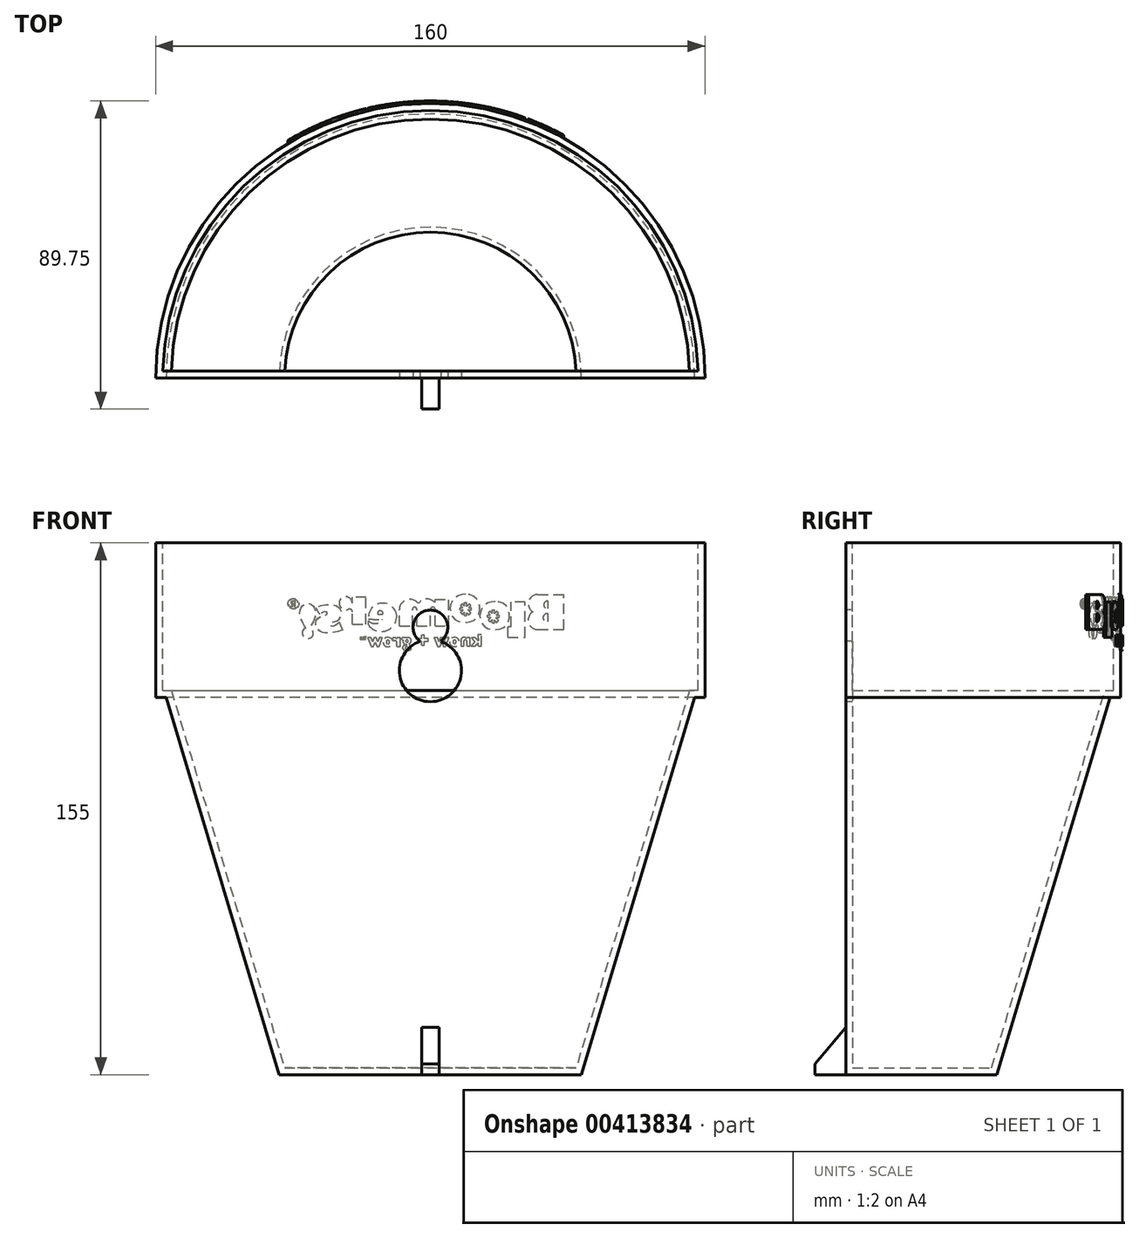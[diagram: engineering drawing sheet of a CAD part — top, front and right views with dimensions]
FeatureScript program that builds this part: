
annotation { "Feature Type Name" : "Feature", "Feature Type Description" : "" }
export const myFeature = defineFeature(function(context is Context, id is Id, definition is map)
    precondition{}
    {
        {
            var Q0;
            Q0=qCreatedBy(makeId("Front.planeOp"),FACE);
            var sketch = newSketch(context, id + "F0", { "sketchPlane" : qUnion([Q0])});
            skLineSegment(sketch, "E0", {"start": v(0, 63.42) * mm, "end": v(-80, 63.42) * mm});
            skLineSegment(sketch, "E1", {"start": v(-80, 63.42) * mm, "end": v(-80, 18.42) * mm});
            skLineSegment(sketch, "E2", {"start": v(0, -91.58) * mm, "end": v(-44, -91.58) * mm});
            skLineSegment(sketch, "E3", {"start": v(-80, 18.42) * mm, "end": v(-77, 18.42) * mm});
            skLineSegment(sketch, "E4", {"start": v(0, 63.42) * mm, "end": v(0, -91.58) * mm});
            skLineSegment(sketch, "E5", {"start": v(-77, 18.42) * mm, "end": v(-44, -91.58) * mm});
            skLineSegment(sketch, "E6.MirrorCS", {"start": v(0, 63.42) * mm, "end": v(80, 63.42) * mm});
            skLineSegment(sketch, "E7.MirrorCS", {"start": v(80, 63.42) * mm, "end": v(80, 18.42) * mm});
            skLineSegment(sketch, "E8.MirrorCS", {"start": v(80, 18.42) * mm, "end": v(77, 18.42) * mm});
            skLineSegment(sketch, "E9.MirrorCS", {"start": v(77, 18.42) * mm, "end": v(44, -91.58) * mm});
            skLineSegment(sketch, "E10.MirrorCS", {"start": v(0, -91.58) * mm, "end": v(44, -91.58) * mm});
            skSolve(sketch);
        }
        {
            var Q0;
            {var subQ0=sQuery(id+"F0.wireOp",EDGE,"E3");Q0=makeQuery(id+"F0.imprint","IMPRINT",FACE,{"disambiguationData":[TD([[makeQuery(id+"F0.imprint","IMPRINT",EDGE,{"derivedFrom":subQ0}),1.0]])]});}
            var Q1;
            {var subQ1=sQuery(id+"F0.wireOp",EDGE,"E0");Q1=makeQuery(id+"F0.imprint","IMPRINT",FACE,{"disambiguationData":[TD([[makeQuery(id+"F0.imprint","IMPRINT",EDGE,{"derivedFrom":subQ1}),1.0]])]});}
            var Q2;
            Q2=makeQuery(id+"F0.imprint","IMPRINT",FACE,{"disambiguationData":[TD([[makeQuery(id+"F0.imprint","IMPRINT",EDGE,{"derivedFrom":sQuery(id+"F0.wireOp",EDGE,"Kfnrekvc-ZjTY-c2iQ-cK4z-hKnBe4uEAVNk")}),1.0]])]});
            var Q3;
            Q3=sQuery(id+"F0.wireOp",EDGE,"E4");
            revolve(context, id + "F1", {"entities" : qUnion([Q0, Q1, Q2]), "axis" : qUnion([Q3]), "revolveType" : RevolveType.ONE_DIRECTION, "angle" : 180 * degree});
        }
        {
            var Q0;
            Q0=makeQuery(id+"FK2OT3XlAi37Aaq_1.splitOp","SPLIT",FACE,{"derivedFrom":makeQuery(id+"F1.opRevolve","SWEPT_FACE",FACE,{"disambiguationData":[OSD([sQuery(id+"F0.wireOp",EDGE,"E0")])]}),"isFromBackBody":true});
            shell(context, id + "F2", {"entities" : qUnion([Q0]), "thickness" : 2 * mm});
        }
        {
            var Q0;
            Q0=qCreatedBy(makeId("Front.planeOp"),FACE);
            var sketch = newSketch(context, id + "F3", { "sketchPlane" : qUnion([Q0])});
            skLineSegment(sketch, "E11.bottom", {"start": v(-2.5, -76.58) * mm, "end": v(2.5, -76.58) * mm});
            skLineSegment(sketch, "E11.top", {"start": v(-2.5, -91.58) * mm, "end": v(2.5, -91.58) * mm});
            skLineSegment(sketch, "E11.left", {"start": v(-2.5, -76.58) * mm, "end": v(-2.5, -91.58) * mm});
            skLineSegment(sketch, "E11.right", {"start": v(2.5, -76.58) * mm, "end": v(2.5, -91.58) * mm});
            skPoint(sketch, "E11.middle", {"position": v(0, -84.08) * mm});
            skSolve(sketch);
        }
        {
            var Q0;
            Q0=qSketchRegion(id+"F3",true);
            extrude(context, id + "F4", {"entities" : qUnion([Q0]), "operationType" : NewBodyOperationType.ADD, "depth" : 9 * mm});
        }
        {
            var Q0;
            Q0=qCreatedBy(makeId("Front.planeOp"),FACE);
            var sketch = newSketch(context, id + "F5", { "sketchPlane" : qUnion([Q0])});
            skCircle(sketch, "E12", {"center": v(0, 38.78) * mm, "radius": 5.05 * mm});
            skCircle(sketch, "E13", {"center": v(0, 26.17) * mm, "radius": 9.05 * mm});
            skSolve(sketch);
        }
        {
            var Q0;
            {var subQ0=sQuery(id+"F5.wireOp",EDGE,"E13");var subQ1=sQuery(id+"F5.wireOp",EDGE,"E12");var subQ2=makeQuery(id+"F5.imprint","INTERSECT",VERTEX,{"disambiguationData":[OD(0.0)],"derivedFrom":[subQ1,subQ0]});Q0=makeQuery(id+"F5.imprint","IMPRINT",FACE,{"disambiguationData":[TD([[makeQuery(id+"F5.imprint","IMPRINT",EDGE,{"disambiguationData":[TD([[subQ2,1.0]])],"derivedFrom":subQ1}),1.0]])]});}
            var Q1;
            {var subQ0=sQuery(id+"F5.wireOp",EDGE,"E13");var subQ1=sQuery(id+"F5.wireOp",EDGE,"E12");var subQ2=makeQuery(id+"F5.imprint","INTERSECT",VERTEX,{"disambiguationData":[OD(0.0)],"derivedFrom":[subQ1,subQ0]});Q1=makeQuery(id+"F5.imprint","IMPRINT",FACE,{"disambiguationData":[TD([[makeQuery(id+"F5.imprint","IMPRINT",EDGE,{"disambiguationData":[TD([[subQ2,-1.0]])],"derivedFrom":subQ1}),-1.0]])]});}
            var Q2;
            {var subQ0=sQuery(id+"F5.wireOp",EDGE,"E13");var subQ1=sQuery(id+"F5.wireOp",EDGE,"E12");var subQ2=makeQuery(id+"F5.imprint","INTERSECT",VERTEX,{"disambiguationData":[OD(0.0)],"derivedFrom":[subQ1,subQ0]});Q2=makeQuery(id+"F5.imprint","IMPRINT",FACE,{"disambiguationData":[TD([[makeQuery(id+"F5.imprint","IMPRINT",EDGE,{"disambiguationData":[TD([[subQ2,-1.0]])],"derivedFrom":subQ1}),1.0]])]});}
            var Q3;
            Q3=sQuery(id+"F5.wireOp",EDGE,"E12");
            var Q4;
            Q4=sQuery(id+"F5.wireOp",EDGE,"E13");
            extrude(context, id + "F6", {"entities" : qUnion([Q0, Q1, Q2]), "operationType" : NewBodyOperationType.REMOVE, "surfaceEntities" : qUnion([Q3, Q4]), "oppositeDirection" : true, "depth" : 10 * mm});
        }
        {
            var Q0;
            Q0=makeQuery(id+"F4.opExtrude","CAP_EDGE",EDGE,{"disambiguationData":[OSD([sQuery(id+"F3.wireOp",EDGE,"E11.bottom")])],"isStart":false});
            chamfer(context, id + "F7", {"entities" : qUnion([Q0]), "chamferType" : ChamferType.OFFSET_ANGLE, "width" : 10 * mm, "oppositeDirection" : false, "angle" : 50 * degree, "tangentPropagation" : true});
        }
        {
            var Q0;
            Q0=makeQuery(id+"F1.opRevolve","SWEPT_BODY",BODY,{"disambiguationData":[OSD([sQuery(id+"F0.wireOp",EDGE,"E0"),sQuery(id+"F0.wireOp",EDGE,"E1"),sQuery(id+"F0.wireOp",EDGE,"E2"),sQuery(id+"F0.wireOp",EDGE,"E3"),sQuery(id+"F0.wireOp",EDGE,"E4"),sQuery(id+"F0.wireOp",EDGE,"E5")])]});
            transform(context, id + "F8", {"entities" : qUnion([Q0]), "transformType" : TransformType.TRANSLATION_3D, "dx" : 0 * mm, "dy" : 0 * mm, "dz" : -7 * mm, "makeCopy" : false});
        }
        {
            var Q0;
            Q0=makeQuery(id+"F2.opShell","OFFSET_FACE",FACE,{"disambiguationData":[OSD([sQuery(id+"F0.wireOp",EDGE,"E0"),sQuery(id+"F0.wireOp",EDGE,"E1"),sQuery(id+"F0.wireOp",EDGE,"E2"),sQuery(id+"F0.wireOp",EDGE,"E3"),sQuery(id+"F0.wireOp",EDGE,"E4"),sQuery(id+"F0.wireOp",EDGE,"E5")])]});
            cPlane(context, id + "F9", {"entities" : qUnion([Q0]), "cplaneType" : CPlaneType.OFFSET, "offset" : 78.9 * mm, "width" : 150 * mm, "height" : 150 * mm});
        }
        {
            var Q0;
            Q0=qCreatedBy(id+"F9.planeOp",FACE);
            var sketch = newSketch(context, id + "F10", { "sketchPlane" : qUnion([Q0])});
            skLineSegment(sketch, "E14", {"start": v(-38.93, 41.35) * mm, "end": v(-38.93, 31.1) * mm});
            skLineSegment(sketch, "E15", {"start": v(-38.93, 31.1) * mm, "end": v(-31.26, 31.1) * mm});
            skLineSegment(sketch, "E16", {"start": v(-38.93, 41.35) * mm, "end": v(-31.26, 41.35) * mm});
            skArc(sketch, "E17", {"start": v(-29.86, 36.3) * mm, "mid": v(-28.64, 39.36) * mm, "end": v(-31.26, 41.35) * mm});
            skArc(sketch, "E18", {"start": v(-31.26, 31.1) * mm, "mid": v(-28.56, 33.17) * mm, "end": v(-29.86, 36.3) * mm});
            skLineSegment(sketch, "E19", {"start": v(-34.3, 39.39) * mm, "end": v(-34.3, 37.24) * mm});
            skArc(sketch, "E20", {"start": v(-34.3, 37.24) * mm, "mid": v(-33, 38.32) * mm, "end": v(-34.3, 39.39) * mm});
            skArc(sketch, "E21", {"start": v(-34.3, 33.47) * mm, "mid": v(-32.82, 34.59) * mm, "end": v(-34.3, 35.7) * mm});
            skLineSegment(sketch, "E22.trimOffspring", {"start": v(-34.3, 35.7) * mm, "end": v(-34.3, 33.47) * mm});
            skLineSegment(sketch, "E23", {"start": v(-27.58, 39.2) * mm, "end": v(-27.58, 28.9) * mm});
            skLineSegment(sketch, "E24", {"start": v(-27.58, 28.9) * mm, "end": v(-22.58, 28.9) * mm});
            skLineSegment(sketch, "E25", {"start": v(-22.58, 28.9) * mm, "end": v(-22.58, 31.98) * mm});
            skLineSegment(sketch, "E26", {"start": v(-22.58, 31.98) * mm, "end": v(-23.52, 31.98) * mm});
            skLineSegment(sketch, "E27", {"start": v(-23.52, 31.98) * mm, "end": v(-23.52, 39.2) * mm});
            skLineSegment(sketch, "E28", {"start": v(-23.52, 39.2) * mm, "end": v(-27.58, 39.2) * mm});
            skFitSpline(sketch, "E29", {"points": [v(-18.97, 39.3) * mm, v(-20.87, 38.92) * mm, v(-22.46, 37.44) * mm, v(-22.99, 35.82) * mm, v(-22.97, 34.09) * mm, v(-22.03, 32.34) * mm, v(-20.21, 31.27) * mm, v(-18.57, 31.14) * mm, v(-16.6, 31.5) * mm, v(-14.9, 33.15) * mm, v(-14.42, 35.37) * mm, v(-14.96, 37.3) * mm, v(-16.45, 38.75) * mm, v(-18.2, 39.28) * mm, v(-18.97, 39.3) * mm]});
            skLineSegment(sketch, "E30.bottom", {"start": v(-18.65, 36.9) * mm, "end": v(-18, 36.9) * mm});
            skLineSegment(sketch, "E30.top", {"start": v(-18.65, 33.13) * mm, "end": v(-18, 33.13) * mm});
            skLineSegment(sketch, "E30.left", {"start": v(-18.65, 36.9) * mm, "end": v(-18.65, 35.74) * mm});
            skLineSegment(sketch, "E30.right", {"start": v(-18, 36.9) * mm, "end": v(-18, 35.82) * mm});
            skLineSegment(sketch, "E31.bottom", {"start": v(-20.04, 35.3) * mm, "end": v(-19.23, 35.3) * mm});
            skLineSegment(sketch, "E31.top", {"start": v(-20.04, 34.7) * mm, "end": v(-19.05, 34.7) * mm});
            skLineSegment(sketch, "E31.left", {"start": v(-20.04, 35.3) * mm, "end": v(-20.04, 34.7) * mm});
            skLineSegment(sketch, "E31.right", {"start": v(-16.69, 35.3) * mm, "end": v(-16.69, 34.7) * mm});
            skLineSegment(sketch, "E32", {"start": v(-19.87, 35.97) * mm, "end": v(-19.23, 35.3) * mm});
            skLineSegment(sketch, "E33", {"start": v(-17.4, 33.43) * mm, "end": v(-16.88, 33.92) * mm});
            skLineSegment(sketch, "E34", {"start": v(-19.35, 36.45) * mm, "end": v(-19.87, 35.97) * mm});
            skLineSegment(sketch, "E35", {"start": v(-19.87, 33.85) * mm, "end": v(-19.25, 33.22) * mm});
            skLineSegment(sketch, "E36", {"start": v(-19.25, 33.22) * mm, "end": v(-18.65, 33.9) * mm});
            skLineSegment(sketch, "E37", {"start": v(-16.84, 35.97) * mm, "end": v(-17.39, 36.45) * mm});
            skLineSegment(sketch, "E38", {"start": v(-17.39, 36.45) * mm, "end": v(-18, 35.82) * mm});
            skLineSegment(sketch, "E39.trimOffspring", {"start": v(-18.65, 35.74) * mm, "end": v(-19.35, 36.45) * mm});
            skLineSegment(sketch, "E40.trimOffspring", {"start": v(-19.05, 34.7) * mm, "end": v(-19.87, 33.85) * mm});
            skLineSegment(sketch, "E41.trimOffspring", {"start": v(-18, 34.04) * mm, "end": v(-17.4, 33.43) * mm});
            skLineSegment(sketch, "E42.trimOffspring", {"start": v(-18.65, 33.9) * mm, "end": v(-18.65, 33.13) * mm});
            skLineSegment(sketch, "E43.trimOffspring", {"start": v(-18, 34.04) * mm, "end": v(-18, 33.13) * mm});
            skLineSegment(sketch, "E44.trimOffspring", {"start": v(-17.42, 35.3) * mm, "end": v(-16.84, 35.97) * mm});
            skLineSegment(sketch, "E45.trimOffspring", {"start": v(-17.42, 35.3) * mm, "end": v(-16.69, 35.3) * mm});
            skLineSegment(sketch, "E46.trimOffspring", {"start": v(-17.65, 34.7) * mm, "end": v(-16.69, 34.7) * mm});
            skFitSpline(sketch, "E47", {"points": [v(-10.3, 41.42) * mm, v(-12.2, 41.04) * mm, v(-13.79, 39.56) * mm, v(-14.32, 37.94) * mm, v(-14.3, 36.2) * mm, v(-13.36, 34.46) * mm, v(-11.55, 33.39) * mm, v(-9.9, 33.26) * mm, v(-7.94, 33.62) * mm, v(-6.23, 35.27) * mm, v(-5.76, 37.49) * mm, v(-6.3, 39.41) * mm, v(-7.79, 40.86) * mm, v(-9.54, 41.4) * mm, v(-10.3, 41.42) * mm]});
            skLineSegment(sketch, "E48", {"start": v(-17.65, 34.7) * mm, "end": v(-16.88, 33.92) * mm});
            skLineSegment(sketch, "E49.bottom", {"start": v(-10.58, 39.06) * mm, "end": v(-9.92, 39.06) * mm});
            skLineSegment(sketch, "E49.top", {"start": v(-10.58, 35.28) * mm, "end": v(-9.92, 35.28) * mm});
            skLineSegment(sketch, "E49.left", {"start": v(-10.58, 39.06) * mm, "end": v(-10.58, 37.9) * mm});
            skLineSegment(sketch, "E49.right", {"start": v(-9.92, 39.06) * mm, "end": v(-9.92, 37.97) * mm});
            skLineSegment(sketch, "E50.bottom", {"start": v(-11.97, 37.46) * mm, "end": v(-11.15, 37.46) * mm});
            skLineSegment(sketch, "E50.top", {"start": v(-11.97, 36.86) * mm, "end": v(-10.98, 36.86) * mm});
            skLineSegment(sketch, "E50.left", {"start": v(-11.97, 37.46) * mm, "end": v(-11.97, 36.86) * mm});
            skLineSegment(sketch, "E50.right", {"start": v(-8.61, 37.46) * mm, "end": v(-8.61, 36.86) * mm});
            skLineSegment(sketch, "E51", {"start": v(-11.8, 38.12) * mm, "end": v(-11.15, 37.46) * mm});
            skLineSegment(sketch, "E52", {"start": v(-9.32, 35.58) * mm, "end": v(-8.81, 36.08) * mm});
            skLineSegment(sketch, "E53", {"start": v(-11.27, 38.6) * mm, "end": v(-11.8, 38.12) * mm});
            skLineSegment(sketch, "E54", {"start": v(-11.8, 36) * mm, "end": v(-11.18, 35.37) * mm});
            skLineSegment(sketch, "E55", {"start": v(-11.18, 35.37) * mm, "end": v(-10.58, 36.05) * mm});
            skLineSegment(sketch, "E56", {"start": v(-8.76, 38.12) * mm, "end": v(-9.31, 38.6) * mm});
            skLineSegment(sketch, "E57", {"start": v(-9.31, 38.6) * mm, "end": v(-9.92, 37.97) * mm});
            skLineSegment(sketch, "E58.trimOffspring", {"start": v(-10.58, 37.9) * mm, "end": v(-11.27, 38.6) * mm});
            skLineSegment(sketch, "E59.trimOffspring", {"start": v(-10.98, 36.86) * mm, "end": v(-11.8, 36) * mm});
            skLineSegment(sketch, "E60.trimOffspring", {"start": v(-9.92, 36.2) * mm, "end": v(-9.32, 35.58) * mm});
            skLineSegment(sketch, "E61.trimOffspring", {"start": v(-10.58, 36.05) * mm, "end": v(-10.58, 35.28) * mm});
            skLineSegment(sketch, "E62.trimOffspring", {"start": v(-9.92, 36.2) * mm, "end": v(-9.92, 35.28) * mm});
            skLineSegment(sketch, "E63.trimOffspring", {"start": v(-9.34, 37.46) * mm, "end": v(-8.76, 38.12) * mm});
            skLineSegment(sketch, "E64.trimOffspring", {"start": v(-9.34, 37.46) * mm, "end": v(-8.61, 37.46) * mm});
            skLineSegment(sketch, "E65.trimOffspring", {"start": v(-9.58, 36.86) * mm, "end": v(-8.61, 36.86) * mm});
            skLineSegment(sketch, "E66", {"start": v(-9.58, 36.86) * mm, "end": v(-8.81, 36.08) * mm});
            skLineSegment(sketch, "E67", {"start": v(-5.38, 32.17) * mm, "end": v(-5.38, 39.97) * mm});
            skLineSegment(sketch, "E68", {"start": v(-5.38, 39.97) * mm, "end": v(-1.39, 39.97) * mm});
            skLineSegment(sketch, "E69", {"start": v(-1.39, 39.97) * mm, "end": v(-1.39, 39) * mm});
            skLineSegment(sketch, "E70", {"start": v(-5.38, 32.17) * mm, "end": v(-1.38, 32.17) * mm});
            skLineSegment(sketch, "E71", {"start": v(-1.38, 32.17) * mm, "end": v(-1.38, 36.98) * mm});
            skLineSegment(sketch, "E72", {"start": v(0, 36.98) * mm, "end": v(0, 32.17) * mm});
            skLineSegment(sketch, "E73", {"start": v(0, 32.17) * mm, "end": v(3.95, 32.17) * mm});
            skLineSegment(sketch, "E74", {"start": v(3.95, 32.17) * mm, "end": v(3.95, 36.98) * mm});
            skLineSegment(sketch, "E75", {"start": v(5.25, 36.98) * mm, "end": v(5.25, 32.17) * mm});
            skLineSegment(sketch, "E76", {"start": v(5.25, 32.17) * mm, "end": v(9.02, 32.17) * mm});
            skLineSegment(sketch, "E77", {"start": v(9.02, 32.17) * mm, "end": v(9.02, 36.98) * mm});
            skArc(sketch, "E78", {"start": v(5.25, 36.98) * mm, "mid": v(4.6, 37.63) * mm, "end": v(3.95, 36.98) * mm});
            skArc(sketch, "E79", {"start": v(0, 36.98) * mm, "mid": v(-0.69, 37.67) * mm, "end": v(-1.38, 36.98) * mm});
            skArc(sketch, "E80", {"start": v(3.53, 38.66) * mm, "mid": v(1.15, 40.01) * mm, "end": v(-1.39, 39) * mm});
            skArc(sketch, "E81", {"start": v(9.02, 36.98) * mm, "mid": v(6.9, 39.85) * mm, "end": v(3.53, 38.66) * mm});
            skArc(sketch, "E82", {"start": v(13.95, 34.1) * mm, "mid": v(15.9, 32.9) * mm, "end": v(18.03, 33.72) * mm});
            skArc(sketch, "E83", {"start": v(9.77, 35.2) * mm, "mid": v(12.91, 30.78) * mm, "end": v(18.06, 32.5) * mm});
            skArc(sketch, "E84", {"start": v(18.03, 34.17) * mm, "mid": v(14.4, 38.8) * mm, "end": v(9.77, 35.2) * mm});
            skLineSegment(sketch, "E85", {"start": v(13.95, 34.1) * mm, "end": v(18.03, 34.17) * mm});
            skLineSegment(sketch, "E86", {"start": v(13.9, 35.57) * mm, "end": v(15.36, 35.6) * mm});
            skArc(sketch, "E87", {"start": v(15.36, 35.6) * mm, "mid": v(14.6, 36.63) * mm, "end": v(13.9, 35.57) * mm});
            skLineSegment(sketch, "E88", {"start": v(18.03, 33.72) * mm, "end": v(18.06, 32.5) * mm});
            skLineSegment(sketch, "E89", {"start": v(22.73, 38.77) * mm, "end": v(22.73, 40.55) * mm});
            skLineSegment(sketch, "E90", {"start": v(22.73, 40.55) * mm, "end": v(18.72, 40.58) * mm});
            skLineSegment(sketch, "E91", {"start": v(18.72, 40.58) * mm, "end": v(18.72, 32.74) * mm});
            skLineSegment(sketch, "E92", {"start": v(18.72, 32.74) * mm, "end": v(22.7, 32.74) * mm});
            skLineSegment(sketch, "E93", {"start": v(22.7, 32.74) * mm, "end": v(22.7, 36.3) * mm});
            skArc(sketch, "E94", {"start": v(23.94, 36.98) * mm, "mid": v(26.24, 39.84) * mm, "end": v(22.73, 38.77) * mm});
            skArc(sketch, "E95", {"start": v(23.94, 36.98) * mm, "mid": v(23.11, 37) * mm, "end": v(22.7, 36.3) * mm});
            skLineSegment(sketch, "E96", {"start": v(33.3, 37.45) * mm, "end": v(32.27, 35.62) * mm});
            skFitSpline(sketch, "E97", {"points": [v(33.3, 37.45) * mm, v(32.36, 37.96) * mm, v(31.25, 38.2) * mm, v(30.16, 38.3) * mm, v(28.65, 38.26) * mm, v(27.14, 37.83) * mm, v(26.29, 37.06) * mm, v(25.86, 36.05) * mm, v(26.07, 34.84) * mm, v(26.79, 33.99) * mm, v(28.33, 33.35) * mm, v(29.12, 33.1) * mm, v(29.36, 32.85) * mm, v(29.3, 32.47) * mm, v(29, 32.12) * mm, v(28.48, 32.1) * mm, v(27.57, 32.38) * mm, v(26.88, 32.96) * mm, v(26.6, 33.22) * mm, v(26.49, 33.3) * mm], "startDerivative": vector(-15.65, 9.87) * mm, "endDerivative": vector(-4.84, 3.4) * mm});
            skFitSpline(sketch, "E98", {"points": [v(32.27, 35.62) * mm, v(31.94, 35.79) * mm, v(31.56, 36.06) * mm, v(31.13, 36.28) * mm, v(30.73, 36.4) * mm, v(30.1, 36.28) * mm, v(29.89, 35.88) * mm, v(30.08, 35.62) * mm, v(30.64, 35.32) * mm, v(31.42, 35.1) * mm, v(32.1, 34.87) * mm, v(32.63, 34.52) * mm, v(33.07, 34.09) * mm, v(33.37, 33.46) * mm, v(33.46, 33) * mm, v(33.46, 32.48) * mm, v(33.31, 31.72) * mm, v(32.8, 31.07) * mm, v(32.27, 30.71) * mm, v(31.46, 30.26) * mm, v(30.44, 30.1) * mm, v(29.25, 30.17) * mm, v(28.56, 30.21) * mm, v(27.53, 30.4) * mm, v(26.65, 30.67) * mm, v(26.13, 30.83) * mm, v(25.52, 31) * mm, v(24, 31.52) * mm], "startDerivative": vector(-12.22, 5.14) * mm, "endDerivative": vector(-29.8, 10.92) * mm});
            skLineSegment(sketch, "E99", {"start": v(26.49, 33.3) * mm, "end": v(25.52, 31) * mm});
            skFitSpline(sketch, "E100", {"points": [v(35.16, 31.53) * mm, v(34.54, 32.68) * mm, v(33.94, 33.8) * mm, v(33.6, 34.86) * mm, v(33.49, 36.06) * mm, v(33.7, 37.34) * mm, v(34.55, 38.4) * mm, v(35.36, 38.83) * mm, v(36.02, 38.89) * mm, v(36.86, 38.44) * mm, v(37.6, 37.54) * mm, v(38.02, 36.55) * mm, v(37.98, 35.4) * mm, v(37.68, 34.14) * mm, v(37.17, 33.21) * mm, v(36.7, 32.27) * mm, v(36.3, 31.56) * mm, v(36.34, 31.34) * mm], "startDerivative": vector(-9.25, 17.51) * mm, "endDerivative": vector(7.08, -5.7) * mm});
            skFitSpline(sketch, "E101", {"points": [v(35.16, 31.53) * mm, v(34.67, 31.23) * mm, v(34.3, 30.83) * mm, v(34.1, 30) * mm, v(34.28, 29.4) * mm, v(34.62, 28.94) * mm, v(35.02, 28.64) * mm, v(35.5, 28.5) * mm, v(36.33, 28.63) * mm, v(37.12, 29.37) * mm, v(37.32, 30.35) * mm, v(37.03, 31) * mm, v(36.66, 31.33) * mm, v(36.3, 31.56) * mm], "startDerivative": vector(-7.2, -4.04) * mm, "endDerivative": vector(-5.92, 3.66) * mm});
            skLineSegment(sketch, "E102", {"start": v(-13.86, 29.67) * mm, "end": v(-14.85, 29.67) * mm});
            skLineSegment(sketch, "E103", {"start": v(-14.85, 29.67) * mm, "end": v(-14.85, 26.29) * mm});
            skLineSegment(sketch, "E104", {"start": v(-14.85, 26.29) * mm, "end": v(-13.95, 26.29) * mm});
            skLineSegment(sketch, "E105", {"start": v(-13.95, 26.29) * mm, "end": v(-13.95, 27.28) * mm});
            skLineSegment(sketch, "E106", {"start": v(-13.95, 27.28) * mm, "end": v(-13.01, 26.29) * mm});
            skLineSegment(sketch, "E107", {"start": v(-13.01, 26.29) * mm, "end": v(-11.85, 26.29) * mm});
            skLineSegment(sketch, "E108", {"start": v(-11.85, 26.29) * mm, "end": v(-12.9, 27.58) * mm});
            skLineSegment(sketch, "E109", {"start": v(-12.9, 27.58) * mm, "end": v(-11.98, 28.72) * mm});
            skLineSegment(sketch, "E110", {"start": v(-11.98, 28.72) * mm, "end": v(-13.1, 28.72) * mm});
            skLineSegment(sketch, "E111", {"start": v(-13.1, 28.72) * mm, "end": v(-13.95, 27.88) * mm});
            skLineSegment(sketch, "E112", {"start": v(-13.95, 27.88) * mm, "end": v(-13.86, 29.67) * mm});
            skLineSegment(sketch, "E113", {"start": v(-11.59, 26.29) * mm, "end": v(-10.62, 26.29) * mm});
            skLineSegment(sketch, "E114", {"start": v(-10.62, 26.29) * mm, "end": v(-10.62, 27.77) * mm});
            skLineSegment(sketch, "E115", {"start": v(-9.77, 27.88) * mm, "end": v(-9.77, 26.29) * mm});
            skLineSegment(sketch, "E116", {"start": v(-9.77, 26.29) * mm, "end": v(-8.9, 26.29) * mm});
            skLineSegment(sketch, "E117", {"start": v(-8.9, 26.29) * mm, "end": v(-8.95, 28.42) * mm});
            skLineSegment(sketch, "E118", {"start": v(-10.49, 28.6) * mm, "end": v(-10.62, 28.6) * mm});
            skLineSegment(sketch, "E119", {"start": v(-10.62, 28.6) * mm, "end": v(-10.62, 28.76) * mm});
            skLineSegment(sketch, "E120", {"start": v(-10.62, 28.76) * mm, "end": v(-11.61, 28.76) * mm});
            skLineSegment(sketch, "E121", {"start": v(-11.61, 28.76) * mm, "end": v(-11.59, 26.29) * mm});
            skEllipse(sketch, "E122", {"center": v(-7.04, 27.54) * mm, "majorRadius": 0.56 * mm, "minorRadius": 0.44 * mm, "majorAxis": v(0, -1)});
            skEllipse(sketch, "E123", {"center": v(-7.04, 27.54) * mm, "majorRadius": 1.33 * mm, "minorRadius": 1.47 * mm, "majorAxis": v(0.05, -1)});
            skLineSegment(sketch, "E124", {"start": v(-4.42, 28.79) * mm, "end": v(-5.45, 28.79) * mm});
            skLineSegment(sketch, "E125", {"start": v(-5.45, 28.79) * mm, "end": v(-4.45, 26.23) * mm});
            skLineSegment(sketch, "E126", {"start": v(-4.45, 26.23) * mm, "end": v(-3.77, 26.23) * mm});
            skLineSegment(sketch, "E127", {"start": v(-3.77, 26.23) * mm, "end": v(-3.28, 27.38) * mm});
            skLineSegment(sketch, "E128", {"start": v(-3.28, 27.38) * mm, "end": v(-2.82, 26.22) * mm});
            skLineSegment(sketch, "E129", {"start": v(-2.82, 26.22) * mm, "end": v(-2.1, 26.22) * mm});
            skLineSegment(sketch, "E130", {"start": v(-2.1, 26.22) * mm, "end": v(-1.1, 28.75) * mm});
            skLineSegment(sketch, "E131", {"start": v(-1.1, 28.75) * mm, "end": v(-2.15, 28.75) * mm});
            skLineSegment(sketch, "E132", {"start": v(-2.15, 28.75) * mm, "end": v(-2.48, 27.64) * mm});
            skLineSegment(sketch, "E133", {"start": v(-2.48, 27.64) * mm, "end": v(-2.9, 28.75) * mm});
            skLineSegment(sketch, "E134", {"start": v(-2.9, 28.75) * mm, "end": v(-3.65, 28.75) * mm});
            skLineSegment(sketch, "E135", {"start": v(-3.65, 28.75) * mm, "end": v(-4.02, 27.66) * mm});
            skLineSegment(sketch, "E136", {"start": v(-4.02, 27.66) * mm, "end": v(-4.42, 28.79) * mm});
            skLineSegment(sketch, "E137", {"start": v(2.5, 29.58) * mm, "end": v(1.8, 29.58) * mm});
            skLineSegment(sketch, "E138", {"start": v(1.8, 29.58) * mm, "end": v(1.8, 28.47) * mm});
            skLineSegment(sketch, "E139", {"start": v(1.8, 28.47) * mm, "end": v(0.59, 28.47) * mm});
            skLineSegment(sketch, "E140", {"start": v(0.59, 28.47) * mm, "end": v(0.59, 27.74) * mm});
            skLineSegment(sketch, "E141", {"start": v(0.59, 27.74) * mm, "end": v(1.77, 27.74) * mm});
            skLineSegment(sketch, "E142", {"start": v(1.77, 27.74) * mm, "end": v(1.77, 26.58) * mm});
            skLineSegment(sketch, "E143", {"start": v(1.77, 26.58) * mm, "end": v(2.5, 26.58) * mm});
            skLineSegment(sketch, "E144", {"start": v(2.5, 26.58) * mm, "end": v(2.5, 27.74) * mm});
            skLineSegment(sketch, "E145", {"start": v(2.5, 27.74) * mm, "end": v(3.63, 27.74) * mm});
            skLineSegment(sketch, "E146", {"start": v(3.63, 27.74) * mm, "end": v(3.63, 28.45) * mm});
            skLineSegment(sketch, "E147", {"start": v(3.63, 28.45) * mm, "end": v(2.5, 28.45) * mm});
            skLineSegment(sketch, "E148", {"start": v(2.5, 28.45) * mm, "end": v(2.5, 29.58) * mm});
            skEllipse(sketch, "E149", {"center": v(12.37, 27.5) * mm, "majorRadius": 0.56 * mm, "minorRadius": 0.47 * mm, "majorAxis": v(0, -1)});
            skEllipse(sketch, "E150", {"center": v(12.37, 27.5) * mm, "majorRadius": 1.38 * mm, "minorRadius": 1.44 * mm, "majorAxis": v(0, -1)});
            skEllipse(sketch, "E151", {"center": v(6.82, 27.81) * mm, "majorRadius": 0.35 * mm, "minorRadius": 0.38 * mm, "majorAxis": v(0, -1)});
            skEllipse(sketch, "E152", {"center": v(6.86, 25.77) * mm, "majorRadius": 0.5 * mm, "minorRadius": 0.27 * mm, "majorAxis": v(1, 0)});
            skLineSegment(sketch, "E153", {"start": v(9.75, 28.76) * mm, "end": v(8.72, 28.76) * mm});
            skLineSegment(sketch, "E154", {"start": v(8.72, 28.76) * mm, "end": v(8.72, 26.23) * mm});
            skLineSegment(sketch, "E155", {"start": v(8.72, 26.23) * mm, "end": v(9.77, 26.23) * mm});
            skLineSegment(sketch, "E156", {"start": v(9.77, 26.23) * mm, "end": v(9.77, 27.57) * mm});
            skLineSegment(sketch, "E157", {"start": v(16.42, 28.76) * mm, "end": v(15.75, 28.76) * mm});
            skLineSegment(sketch, "E158", {"start": v(15.75, 28.76) * mm, "end": v(15.33, 27.62) * mm});
            skLineSegment(sketch, "E159", {"start": v(15.33, 27.62) * mm, "end": v(14.91, 28.77) * mm});
            skLineSegment(sketch, "E160", {"start": v(14.91, 28.77) * mm, "end": v(14, 28.77) * mm});
            skLineSegment(sketch, "E161", {"start": v(14, 28.77) * mm, "end": v(14.91, 26.25) * mm});
            skLineSegment(sketch, "E162", {"start": v(14.91, 26.25) * mm, "end": v(15.58, 26.25) * mm});
            skLineSegment(sketch, "E163", {"start": v(15.58, 26.25) * mm, "end": v(16.06, 27.35) * mm});
            skLineSegment(sketch, "E164", {"start": v(16.06, 27.35) * mm, "end": v(16.6, 26.24) * mm});
            skLineSegment(sketch, "E165", {"start": v(16.6, 26.24) * mm, "end": v(17.25, 26.24) * mm});
            skLineSegment(sketch, "E166", {"start": v(17.25, 26.24) * mm, "end": v(18.26, 28.77) * mm});
            skLineSegment(sketch, "E167", {"start": v(18.26, 28.77) * mm, "end": v(17.24, 28.77) * mm});
            skLineSegment(sketch, "E168", {"start": v(17.24, 28.77) * mm, "end": v(16.82, 27.63) * mm});
            skLineSegment(sketch, "E169", {"start": v(16.82, 27.63) * mm, "end": v(16.42, 28.76) * mm});
            skArc(sketch, "E170", {"start": v(-9.77, 27.88) * mm, "mid": v(-10.23, 28.08) * mm, "end": v(-10.62, 27.77) * mm});
            skArc(sketch, "E171", {"start": v(-8.95, 28.42) * mm, "mid": v(-9.68, 28.85) * mm, "end": v(-10.49, 28.6) * mm});
            skLineSegment(sketch, "E172", {"start": v(9.75, 28.76) * mm, "end": v(9.75, 28.32) * mm});
            skLineSegment(sketch, "E173", {"start": v(10.97, 28.72) * mm, "end": v(10.69, 27.75) * mm});
            skArc(sketch, "E174", {"start": v(10.97, 28.72) * mm, "mid": v(10.29, 28.75) * mm, "end": v(9.75, 28.32) * mm});
            skArc(sketch, "E175", {"start": v(10.69, 27.75) * mm, "mid": v(10.2, 27.84) * mm, "end": v(9.77, 27.57) * mm});
            skLineSegment(sketch, "E176", {"start": v(8.25, 28.14) * mm, "end": v(8.25, 28.77) * mm});
            skLineSegment(sketch, "E177", {"start": v(8.25, 28.77) * mm, "end": v(6.33, 28.77) * mm});
            skArc(sketch, "E178", {"start": v(6.33, 28.77) * mm, "mid": v(5.61, 27.95) * mm, "end": v(6.19, 27.03) * mm});
            skArc(sketch, "E179", {"start": v(6.83, 26.9) * mm, "mid": v(7.8, 27.15) * mm, "end": v(7.96, 28.14) * mm});
            skLineSegment(sketch, "E180", {"start": v(7.96, 28.14) * mm, "end": v(8.25, 28.14) * mm});
            skLineSegment(sketch, "E181", {"start": v(6.83, 26.9) * mm, "end": v(6.83, 26.6) * mm});
            skLineSegment(sketch, "E182", {"start": v(6.83, 26.6) * mm, "end": v(7.57, 26.6) * mm});
            skArc(sketch, "E183", {"start": v(6.19, 27.03) * mm, "mid": v(5.96, 26.73) * mm, "end": v(6.04, 26.36) * mm});
            skArc(sketch, "E184", {"start": v(6.04, 26.36) * mm, "mid": v(5.52, 25.75) * mm, "end": v(6.04, 25.14) * mm});
            skArc(sketch, "E185", {"start": v(7.57, 25.14) * mm, "mid": v(8.09, 25.87) * mm, "end": v(7.57, 26.6) * mm});
            skArc(sketch, "E186", {"start": v(6.04, 25.14) * mm, "mid": v(6.8, 25.03) * mm, "end": v(7.57, 25.14) * mm});
            skText(sketch, "E187", { "text": "TM", "fontName": "OpenSans-Regular.ttf"});
            skCircle(sketch, "E188", {"center": v(39.92, 38.65) * mm, "radius": 1.58 * mm});
            skCircle(sketch, "E189", {"center": v(39.92, 38.65) * mm, "radius": 1.4 * mm});
            const initialGuessF10  = {"E187": [0.0186, 0.02816, 1, 0, 0.0009]};
            skSetInitialGuess(sketch, initialGuessF10);
            skSolve(sketch);
        }
        {
            var Q0;
            Q0=qSketchRegion(id+"F10",true);
            extrude(context, id + "F11", {"entities" : qUnion([Q0]), "operationType" : NewBodyOperationType.ADD, "endBound" : BoundingType.UP_TO_NEXT, "oppositeDirection" : true, "depth" : 25 * mm});
        }
        {
            var Q0;
            Q0=qCreatedBy(id+"F9.planeOp",FACE);
            var sketch = newSketch(context, id + "F12", { "sketchPlane" : qUnion([Q0])});
            skText(sketch, "E190", { "text": "R", "fontName": "OpenSans-Regular.ttf"});
            const initialGuessF12  = {"E190": [0.03904, 0.03769, 1, 0, 0.0019]};
            skSetInitialGuess(sketch, initialGuessF12);
            skSolve(sketch);
        }
        {
            var Q0;
            Q0=qSketchRegion(id+"F12",true);
            extrude(context, id + "F13", {"entities" : qUnion([Q0]), "operationType" : NewBodyOperationType.ADD, "endBound" : BoundingType.UP_TO_NEXT, "oppositeDirection" : true, "depth" : 25 * mm});
        }
        {
            var Q0;
            Q0=makeQuery(id+"F1.opRevolve","SWEPT_FACE",FACE,{"disambiguationData":[OSD([sQuery(id+"F0.wireOp",EDGE,"E0")])]});
            var sketch = newSketch(context, id + "F14", { "sketchPlane" : qUnion([Q0])});
            skCircle(sketch, "E191", {"center": v(0, 0) * mm, "radius": 80.75 * mm});
            skCircle(sketch, "E192", {"center": v(0, 0) * mm, "radius": 100 * mm});
            skSolve(sketch);
        }
        {
            var Q0;
            Q0=qSketchRegion(id+"F14",true);
            extrude(context, id + "F15", {"entities" : qUnion([Q0]), "operationType" : NewBodyOperationType.REMOVE, "oppositeDirection" : true, "depth" : 124 * mm});
        }
    });
